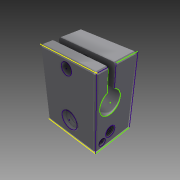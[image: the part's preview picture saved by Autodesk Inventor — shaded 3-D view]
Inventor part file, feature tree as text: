
AUTODESK INVENTOR PART (.ipt)
format: ipt  version: 2015 (Build 190159000, 159)  size: 397,312 bytes
history: native  units: mm
features: sketch x4, hole x4, other x3, extrude x2, chamfer x1
ambient origin geometry x8: Origin, YZ Plane, XZ Plane, XY Plane, X Axis, Y Axis, Z Axis, Center Point
bodies: Body1 (feature_tree)
feature tree (14):
  other  "Твердое тело1"
  extrude  "Выдавливание1"  Depth=3.025mm
  sketch  "Эскиз2"
  hole  "Отверстие1"  [1 undecoded]
  hole  "Отверстие3"  [1 undecoded]
  hole  "Отверстие4"  [1 undecoded]
  sketch  "Эскиз3"
  hole  "Отверстие2"  [1 undecoded]
  extrude  "Выдавливание4"  Depth=4.0mm
  chamfer  "Фаска1"  Distance=16.0mm
  other  "РабПлоскость2"
  other  "Пружина2"
  sketch  "Эскиз1"
  sketch  "Эскиз5"
note: 4 required parameter values undecoded (feature->parameter linkage not recoverable at this tier; creation-order binding heuristic only, values carry confidence <= 0.55)
